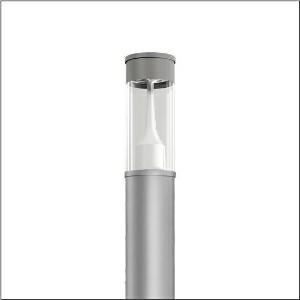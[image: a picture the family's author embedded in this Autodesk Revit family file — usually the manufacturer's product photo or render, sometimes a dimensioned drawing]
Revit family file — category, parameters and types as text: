
# Revit family: city-light_260_iq___pl1_2s_5xa5295cf14h_efd3
name_source: partatom
category: Lighting Fixtures
units: mm (PartAtom-declared; Revit-internal decimal feet)

## family parameters
Cut with Voids When Loaded = No
Host = Face
Light Source = No
Part Type = Normal
Room Calculation Point = No
Round Connector Dimension = Use Diameter
Shared = No

## types (1)
- --- (1 x LED, 2970 lm, 23.9 W, 2200K)
    Apparent Load = 24 VA
    CIE Flux Codes = 23 62 94 96 100
    Color Rendering = 70
    Color Temperature = 2200K
    Default Elevation = 1800 mm
    Description = City-Light 260 iQ, light pillar, Module 540 iQ-SR, primary light control with 3 zone facetted reflector, of plastic, silver coated, highly specular, structured, primary optical cover: cover, of PMMA, transparent, partly coated, light distribution: PL1.2s, primary light characteristic: symmetric, LED, High Power LED, rated luminous flux: 2.970lm, luminous efficacy: 124lm/W, light colour: 722, colour temperature: 2200K, control gear: iQ Street-Remote, control: pre-setting: logarithmic dimming characteristic, Street-Remote, Auto-Match, Temp-Guard, Lumen-Switch, Night-Set, Smart-Wire, Light-Fading, Desk-Remote (wireless, voltage-free reading and setting of iQ features in the workshop via application-optimized NFC function/RFID function), optimised constant luminous flux control (CLO 2.0), with terminal, 6-pole, max. 2.5mm², mains connection: 230..240V, AC, 50/60Hz, start of lifetime: 24W, end of service life: 26W, reduction: 12W, luminaire housing, cylindrical, of extruded aluminium section, coated, Siteco® metallic grey (DB 702S), length: 2.600mm, diameter: 200mm, Module 540 iQ-SR, traffic white (RAL 9016), equipment: standard, protection rating (complete): IP65, insulation class (complete): insulation class II (safety insulation), certification: CE, ENEC, VDE, packaging unit: 1 piece

Light Distribution: PL1.2s
    Height = 500 mm
    Lamp = 1 x LED
    Lamp Light Flux = 2970 lm
    Lamp Power = 23.9 W
    Lamp count = 1
    Length = 200 mm
    Luminous efficacy = 124 lm/W
    Manufacturer = Siteco
    ModVariant = No
    Model = 5XA5295CF14H
    Mounting Place = Floor
    Mounting Type = Freestanding
    Number of Poles = 1
    OnlyDefault = Yes
    Power Factor = 1
    Product Name = City-Light 260 iQ | PL1.2s
    Product group = light pillar
    ProductGroupID = 1301
    Protection Class = Protection class II
    Protection Degree = IP 65
    RLX_Detail_Level = 1
    RLX_Emergency_Light_Flux = 0 lm
    RLX_Emergency_Type = 0
    RLX_Emergency_Type_DB = No
    RlxData = <blob elided: 22037 chars, md5=b8668b3f>
    Socket = socket
    Standby Power = 0 W
    System Light Flux = 2970 lm
    System Power = 24 W
    Type Comments = factory setting: luminous flux: 100 % | dim-lin: 254 | 499 mA
    Type Image = l_1006920.jpg
    URL = http://relux.com
    VarID = @adj_145084
    Voltage = 0 V
    Weight = 0.00 kg
    Width = 0 mm  [stored 0 ft]

note: [stored X ft] marks values corroborated as IEEE doubles in the binary element streams (Revit-internal decimal feet)

## geometry (parser evidence)
native form markers: Blend x4, Sweep x10
no freeform markers — native parametric forms only
